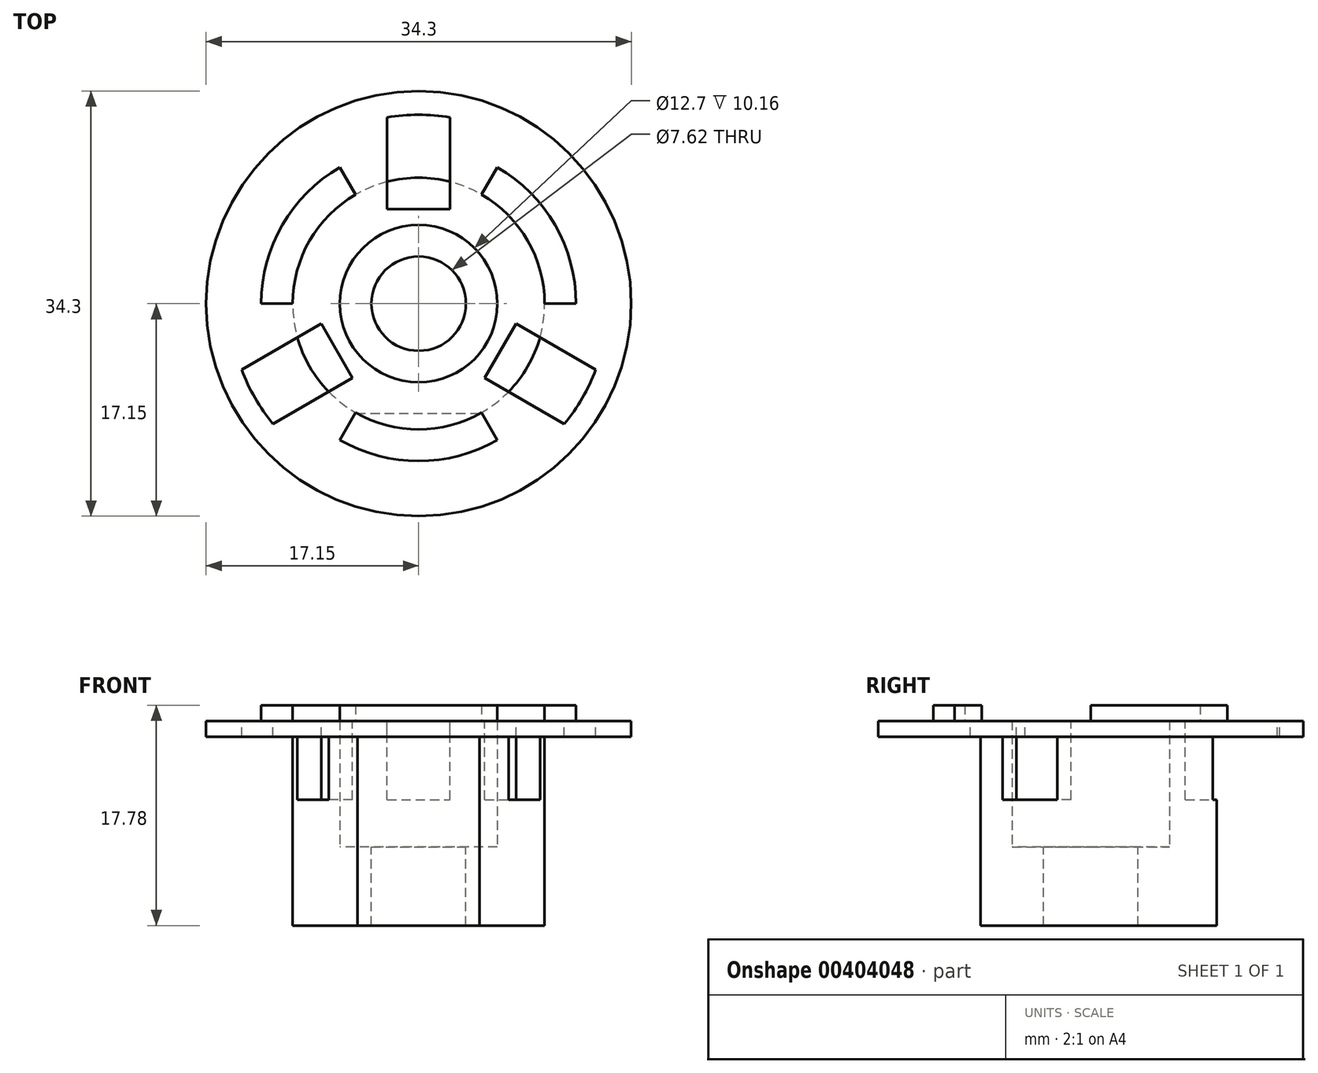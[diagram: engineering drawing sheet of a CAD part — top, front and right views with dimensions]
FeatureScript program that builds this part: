
annotation { "Feature Type Name" : "Feature", "Feature Type Description" : "" }
export const myFeature = defineFeature(function(context is Context, id is Id, definition is map)
    precondition{}
    {
        {
            var Q0;
            Q0=qCreatedBy(makeId("Top.planeOp"),FACE);
            var sketch = newSketch(context, id + "F0", { "sketchPlane" : qUnion([Q0])});
            skCircle(sketch, "E0", {"center": v(0, 0) * mm, "radius": 17.15 * mm});
            skCircle(sketch, "E1", {"center": v(0, 0) * mm, "radius": 6.35 * mm});
            skPoint(sketch, "E2", {"position": v(0, 8.9) * mm});
            skLineSegment(sketch, "E3.bottom", {"start": v(0, 8.9) * mm, "end": v(-2.54, 8.9) * mm});
            skLineSegment(sketch, "E3.top", {"start": v(0, 24.8) * mm, "end": v(-2.54, 24.8) * mm});
            skLineSegment(sketch, "E3.left", {"start": v(0, 8.9) * mm, "end": v(0, 24.8) * mm});
            skLineSegment(sketch, "E3.right", {"start": v(-2.54, 8.9) * mm, "end": v(-2.54, 24.8) * mm});
            skLineSegment(sketch, "E4.bottom", {"start": v(0, 8.9) * mm, "end": v(2.54, 8.9) * mm});
            skLineSegment(sketch, "E4.top", {"start": v(0, 24.8) * mm, "end": v(2.54, 24.8) * mm});
            skLineSegment(sketch, "E4.right", {"start": v(2.54, 8.9) * mm, "end": v(2.54, 24.8) * mm});
            skLineSegment(sketch, "E5.1.0", {"start": v(-6.43, -6.64) * mm, "end": v(-20.2, -14.6) * mm});
            skLineSegment(sketch, "E5.1.1", {"start": v(-21.47, -12.4) * mm, "end": v(-20.2, -14.6) * mm});
            skLineSegment(sketch, "E5.1.2", {"start": v(-21.47, -12.4) * mm, "end": v(-22.74, -10.2) * mm});
            skLineSegment(sketch, "E5.1.3", {"start": v(-8.97, -2.25) * mm, "end": v(-22.74, -10.2) * mm});
            skLineSegment(sketch, "E5.1.4", {"start": v(-7.7, -4.45) * mm, "end": v(-8.97, -2.25) * mm});
            skLineSegment(sketch, "E5.1.5", {"start": v(-7.7, -4.45) * mm, "end": v(-6.43, -6.64) * mm});
            skLineSegment(sketch, "E5.2.0", {"start": v(8.97, -2.25) * mm, "end": v(22.74, -10.2) * mm});
            skLineSegment(sketch, "E5.2.1", {"start": v(21.47, -12.4) * mm, "end": v(22.74, -10.2) * mm});
            skLineSegment(sketch, "E5.2.2", {"start": v(21.47, -12.4) * mm, "end": v(20.2, -14.6) * mm});
            skLineSegment(sketch, "E5.2.3", {"start": v(6.43, -6.64) * mm, "end": v(20.2, -14.6) * mm});
            skLineSegment(sketch, "E5.2.4", {"start": v(7.7, -4.44) * mm, "end": v(6.43, -6.64) * mm});
            skLineSegment(sketch, "E5.2.5", {"start": v(7.7, -4.44) * mm, "end": v(8.97, -2.25) * mm});
            skSolve(sketch);
        }
        {
            var Q0;
            Q0=makeQuery(id+"F0.imprint","IMPRINT",FACE,{"disambiguationData":[TD([[makeQuery(id+"F0.imprint","IMPRINT",EDGE,{"derivedFrom":sQuery(id+"F0.wireOp",EDGE,"E1")}),-1.0]])]});
            extrude(context, id + "F1", {"entities" : qUnion([Q0]), "depth" : 1.27 * mm});
        }
        {
            var Q0;
            Q0=makeQuery(id+"F1.opExtrude","CAP_FACE",FACE,{"disambiguationData":[OSD([sQuery(id+"F0.wireOp",EDGE,"E0"),sQuery(id+"F0.wireOp",EDGE,"E1"),sQuery(id+"F0.wireOp",EDGE,"E3.bottom"),sQuery(id+"F0.wireOp",EDGE,"E3.right"),sQuery(id+"F0.wireOp",EDGE,"E4.bottom"),sQuery(id+"F0.wireOp",EDGE,"E4.right"),sQuery(id+"F0.wireOp",EDGE,"E5.1.0"),sQuery(id+"F0.wireOp",EDGE,"E5.1.3"),sQuery(id+"F0.wireOp",EDGE,"E5.1.4"),sQuery(id+"F0.wireOp",EDGE,"E5.1.5"),sQuery(id+"F0.wireOp",EDGE,"E5.2.0"),sQuery(id+"F0.wireOp",EDGE,"E5.2.3"),sQuery(id+"F0.wireOp",EDGE,"E5.2.4"),sQuery(id+"F0.wireOp",EDGE,"E5.2.5")])],"isStart":true});
            var sketch = newSketch(context, id + "F2", { "sketchPlane" : qUnion([Q0])});
            skCircle(sketch, "E6", {"center": v(0, 0) * mm, "radius": 6.35 * mm});
            skCircle(sketch, "E7", {"center": v(0, 0) * mm, "radius": 10.16 * mm});
            skPoint(sketch, "E8", {"position": v(-2.54, -7.62) * mm});
            skLineSegment(sketch, "E9.bottom", {"start": v(-2.54, -7.62) * mm, "end": v(2.54, -7.62) * mm});
            skLineSegment(sketch, "E9.top", {"start": v(-2.54, -12.48) * mm, "end": v(2.54, -12.48) * mm});
            skLineSegment(sketch, "E9.left", {"start": v(-2.54, -7.62) * mm, "end": v(-2.54, -12.48) * mm});
            skLineSegment(sketch, "E9.right", {"start": v(2.54, -7.62) * mm, "end": v(2.54, -12.48) * mm});
            skLineSegment(sketch, "E10.1.0", {"start": v(7.87, 1.61) * mm, "end": v(5.33, 6) * mm});
            skLineSegment(sketch, "E10.1.1", {"start": v(7.87, 1.61) * mm, "end": v(12.07, 4.04) * mm});
            skLineSegment(sketch, "E10.1.2", {"start": v(12.07, 4.04) * mm, "end": v(9.53, 8.44) * mm});
            skLineSegment(sketch, "E10.1.3", {"start": v(5.33, 6) * mm, "end": v(9.53, 8.44) * mm});
            skLineSegment(sketch, "E10.2.0", {"start": v(-5.33, 6) * mm, "end": v(-7.87, 1.61) * mm});
            skLineSegment(sketch, "E10.2.1", {"start": v(-5.33, 6) * mm, "end": v(-9.53, 8.44) * mm});
            skLineSegment(sketch, "E10.2.2", {"start": v(-9.53, 8.44) * mm, "end": v(-12.07, 4.04) * mm});
            skLineSegment(sketch, "E10.2.3", {"start": v(-7.87, 1.61) * mm, "end": v(-12.07, 4.04) * mm});
            skSolve(sketch);
        }
        {
            var Q0;
            Q0=makeQuery(id+"F2.imprint","IMPRINT",FACE,{"disambiguationData":[TD([[makeQuery(id+"F2.imprint","IMPRINT",EDGE,{"derivedFrom":sQuery(id+"F2.wireOp",EDGE,"E6")}),1.0]])]});
            extrude(context, id + "F3", {"entities" : qUnion([Q0]), "operationType" : NewBodyOperationType.ADD, "depth" : 5.08 * mm});
        }
        {
            var Q0;
            Q0=makeQuery(id+"F3.opExtrude","CAP_FACE",FACE,{"disambiguationData":[OSD([sQuery(id+"F2.wireOp",EDGE,"E6"),sQuery(id+"F2.wireOp",EDGE,"E7"),sQuery(id+"F2.wireOp",EDGE,"E9.bottom"),sQuery(id+"F2.wireOp",EDGE,"E9.left"),sQuery(id+"F2.wireOp",EDGE,"E9.right"),sQuery(id+"F2.wireOp",EDGE,"E10.1.0"),sQuery(id+"F2.wireOp",EDGE,"E10.1.1"),sQuery(id+"F2.wireOp",EDGE,"E10.1.3"),sQuery(id+"F2.wireOp",EDGE,"E10.2.0"),sQuery(id+"F2.wireOp",EDGE,"E10.2.1"),sQuery(id+"F2.wireOp",EDGE,"E10.2.3")])],"isStart":false});
            var sketch = newSketch(context, id + "F4", { "sketchPlane" : qUnion([Q0])});
            skSolve(sketch);
        }
        {
            var Q0;
            Q0=makeQuery(id+"F4.imprint","IMPRINT",FACE,{"disambiguationData":[TD([[makeQuery(id+"F4.imprint","IMPRINT",EDGE,{"derivedFrom":makeQuery(id+"F3.opExtrude","CAP_EDGE",EDGE,{"disambiguationData":[OSD([sQuery(id+"F2.wireOp",EDGE,"E6")])],"isStart":false})}),1.0]])]});
            var sketch = newSketch(context, id + "F5", { "sketchPlane" : qUnion([Q0])});
            skCircle(sketch, "E11", {"center": v(0, 0) * mm, "radius": 6.35 * mm});
            skCircle(sketch, "E12", {"center": v(0, 0) * mm, "radius": 10.16 * mm});
            skSolve(sketch);
        }
        {
            var Q0;
            Q0=makeQuery(id+"F4.imprint","IMPRINT",FACE,{"disambiguationData":[TD([[makeQuery(id+"F4.imprint","IMPRINT",EDGE,{"derivedFrom":makeQuery(id+"F3.opExtrude","CAP_EDGE",EDGE,{"disambiguationData":[OSD([sQuery(id+"F2.wireOp",EDGE,"E6")])],"isStart":false})}),1.0]])]});
            var Q1;
            Q1=makeQuery(id+"F5.imprint","IMPRINT",FACE,{"disambiguationData":[TD([[makeQuery(id+"F5.imprint","IMPRINT",EDGE,{"derivedFrom":makeQuery(id+"F4.imprint","IMPRINT",EDGE,{"derivedFrom":makeQuery(id+"F3.opExtrude","CAP_EDGE",EDGE,{"disambiguationData":[OSD([sQuery(id+"F2.wireOp",EDGE,"E10.2.0")])],"isStart":false})})}),-1.0]])]});
            var Q2;
            Q2=makeQuery(id+"F5.imprint","IMPRINT",FACE,{"disambiguationData":[TD([[makeQuery(id+"F5.imprint","IMPRINT",EDGE,{"derivedFrom":makeQuery(id+"F4.imprint","IMPRINT",EDGE,{"derivedFrom":makeQuery(id+"F3.opExtrude","CAP_EDGE",EDGE,{"disambiguationData":[OSD([sQuery(id+"F2.wireOp",EDGE,"E10.1.0")])],"isStart":false})})}),-1.0]])]});
            var Q3;
            Q3=makeQuery(id+"F5.imprint","IMPRINT",FACE,{"disambiguationData":[TD([[makeQuery(id+"F5.imprint","IMPRINT",EDGE,{"derivedFrom":makeQuery(id+"F4.imprint","IMPRINT",EDGE,{"derivedFrom":makeQuery(id+"F3.opExtrude","CAP_EDGE",EDGE,{"disambiguationData":[OSD([sQuery(id+"F2.wireOp",EDGE,"E9.bottom")])],"isStart":false})})}),-1.0]])]});
            extrude(context, id + "F6", {"entities" : qUnion([Q0, Q1, Q2, Q3]), "operationType" : NewBodyOperationType.ADD, "depth" : 3.8 * mm});
        }
        {
            var Q0;
            {var subQ0=sQuery(id+"F5.wireOp",EDGE,"E12");var subQ1=sQuery(id+"F2.wireOp",EDGE,"E9.right");var subQ2=sQuery(id+"F2.wireOp",EDGE,"E9.left");var subQ3=sQuery(id+"F2.wireOp",EDGE,"E9.bottom");var subQ4=sQuery(id+"F2.wireOp",EDGE,"E10.2.3");var subQ5=sQuery(id+"F2.wireOp",EDGE,"E10.2.1");var subQ6=sQuery(id+"F2.wireOp",EDGE,"E10.2.0");var subQ7=sQuery(id+"F2.wireOp",EDGE,"E10.1.3");var subQ8=sQuery(id+"F2.wireOp",EDGE,"E10.1.1");var subQ9=sQuery(id+"F2.wireOp",EDGE,"E10.1.0");Q0=makeQuery(id+"F6.boolean.opBoolean","MERGE",FACE,{"derivedFrom":[makeQuery(id+"F6.opExtrude","CAP_FACE",FACE,{"disambiguationData":[OSD([sQuery(id+"F2.wireOp",EDGE,"E6"),sQuery(id+"F2.wireOp",EDGE,"E7"),subQ3,subQ2,subQ1,subQ9,subQ8,subQ7,subQ6,subQ5,subQ4])],"isStart":false}),makeQuery(id+"F6.opExtrude","CAP_FACE",FACE,{"disambiguationData":[OSD([subQ9,subQ8,subQ7,subQ0])],"isStart":false}),makeQuery(id+"F6.opExtrude","CAP_FACE",FACE,{"disambiguationData":[OSD([subQ6,subQ5,subQ4,subQ0])],"isStart":false}),makeQuery(id+"F6.opExtrude","CAP_FACE",FACE,{"disambiguationData":[OSD([subQ3,subQ2,subQ1,subQ0])],"isStart":false})]});}
            var sketch = newSketch(context, id + "F7", { "sketchPlane" : qUnion([Q0])});
            skCircle(sketch, "E13", {"center": v(0, 0) * mm, "radius": 3.81 * mm});
            skCircle(sketch, "E14", {"center": v(0, 0) * mm, "radius": 10.16 * mm});
            skSolve(sketch);
        }
        {
            var Q0;
            Q0=makeQuery(id+"F7.imprint","IMPRINT",FACE,{"disambiguationData":[TD([[makeQuery(id+"F7.imprint","IMPRINT",EDGE,{"derivedFrom":sQuery(id+"F7.wireOp",EDGE,"E13")}),-1.0]])]});
            var Q1;
            Q1=makeQuery(id+"F7.imprint","IMPRINT",FACE,{"disambiguationData":[TD([[makeQuery(id+"F7.imprint","IMPRINT",EDGE,{"derivedFrom":sQuery(id+"F7.wireOp",EDGE,"E14")}),1.0]])]});
            extrude(context, id + "F8", {"entities" : qUnion([Q0, Q1]), "operationType" : NewBodyOperationType.ADD, "depth" : 6.35 * mm});
        }
        {
            var Q0;
            Q0=makeQuery(id+"F8.opExtrude","CAP_FACE",FACE,{"disambiguationData":[OSD([sQuery(id+"F7.wireOp",EDGE,"E13"),sQuery(id+"F7.wireOp",EDGE,"E14")])],"isStart":false});
            var sketch = newSketch(context, id + "F9", { "sketchPlane" : qUnion([Q0])});
            skLineSegment(sketch, "E15.bottom", {"start": v(12.8, 8.9) * mm, "end": v(-12.8, 8.9) * mm});
            skLineSegment(sketch, "E15.top", {"start": v(12.8, 11.43) * mm, "end": v(-12.8, 11.43) * mm});
            skLineSegment(sketch, "E15.left", {"start": v(12.8, 8.9) * mm, "end": v(12.8, 11.43) * mm});
            skLineSegment(sketch, "E15.right", {"start": v(-12.8, 8.9) * mm, "end": v(-12.8, 11.43) * mm});
            skPoint(sketch, "E15.middle", {"position": v(0, 10.16) * mm});
            skSolve(sketch);
        }
        {
            var Q0;
            Q0=makeQuery(id+"F9.imprint","IMPRINT",FACE,{"disambiguationData":[TD([[makeQuery(id+"F9.imprint","IMPRINT",EDGE,{"derivedFrom":sQuery(id+"F9.wireOp",EDGE,"E15.top")}),1.0]])]});
            var Q1;
            {var subQ0=sQuery(id+"F9.wireOp",EDGE,"E15.bottom");var subQ1=makeQuery(id+"F8.opExtrude","CAP_EDGE",EDGE,{"disambiguationData":[OSD([sQuery(id+"F7.wireOp",EDGE,"E14")])],"isStart":false});var subQ2=makeQuery(id+"F9.imprint","INTERSECT",VERTEX,{"disambiguationData":[OD(0.0)],"derivedFrom":[subQ1,subQ0]});Q1=makeQuery(id+"F9.imprint","IMPRINT",FACE,{"disambiguationData":[TD([[makeQuery(id+"F9.imprint","IMPRINT",EDGE,{"disambiguationData":[TD([[subQ2,-1.0]])],"derivedFrom":subQ0}),-1.0]])]});}
            var Q2;
            {var subQ3=sQuery(id+"F0.wireOp",EDGE,"E5.1.0");var subQ4=sQuery(id+"F0.wireOp",EDGE,"E5.2.3");var subQ5=sQuery(id+"F0.wireOp",EDGE,"E0");Q2=makeQuery(id+"F3.boolean.opBoolean","SPLIT",FACE,{"disambiguationData":[TD([makeQuery(id+"F1.opExtrude","SWEPT_FACE",FACE,{"disambiguationData":[OSD([subQ5]),TDD([makeQuery(id+"F0.imprint","IMPRINT",EDGE,{"disambiguationData":[TD([[makeQuery(id+"F0.imprint","INTERSECT",VERTEX,{"derivedFrom":[subQ5,subQ3]}),-1.0]])],"derivedFrom":subQ5})])]})])],"derivedFrom":makeQuery(id+"F1.opExtrude","CAP_FACE",FACE,{"disambiguationData":[OSD([subQ5,sQuery(id+"F0.wireOp",EDGE,"E1"),sQuery(id+"F0.wireOp",EDGE,"E3.bottom"),sQuery(id+"F0.wireOp",EDGE,"E3.right"),sQuery(id+"F0.wireOp",EDGE,"E4.bottom"),sQuery(id+"F0.wireOp",EDGE,"E4.right"),subQ3,sQuery(id+"F0.wireOp",EDGE,"E5.1.3"),sQuery(id+"F0.wireOp",EDGE,"E5.1.4"),sQuery(id+"F0.wireOp",EDGE,"E5.1.5"),sQuery(id+"F0.wireOp",EDGE,"E5.2.0"),subQ4,sQuery(id+"F0.wireOp",EDGE,"E5.2.4"),sQuery(id+"F0.wireOp",EDGE,"E5.2.5")])],"isStart":true})});}
            extrude(context, id + "F10", {"entities" : qUnion([Q0, Q1]), "operationType" : NewBodyOperationType.REMOVE, "endBound" : BoundingType.UP_TO_SURFACE, "oppositeDirection" : true, "endBoundEntityFace" : qUnion([Q2]), "depth" : 25.4 * mm});
        }
        {
            var Q0;
            {var subQ0=sQuery(id+"F0.wireOp",EDGE,"E3.right");var subQ1=sQuery(id+"F0.wireOp",EDGE,"E4.right");var subQ2=sQuery(id+"F0.wireOp",EDGE,"E4.bottom");var subQ3=sQuery(id+"F0.wireOp",EDGE,"E3.bottom");Q0=makeQuery(id+"F3.boolean.opBoolean","SPLIT",FACE,{"disambiguationData":[TD([makeQuery(id+"F3.opExtrude","SWEPT_FACE",FACE,{"disambiguationData":[OSD([sQuery(id+"F2.wireOp",EDGE,"E9.bottom")])]})])],"derivedFrom":makeQuery(id+"F1.opExtrude","CAP_FACE",FACE,{"disambiguationData":[OSD([sQuery(id+"F0.wireOp",EDGE,"E0"),sQuery(id+"F0.wireOp",EDGE,"E1"),subQ3,subQ0,subQ2,subQ1,sQuery(id+"F0.wireOp",EDGE,"E5.1.0"),sQuery(id+"F0.wireOp",EDGE,"E5.1.3"),sQuery(id+"F0.wireOp",EDGE,"E5.1.4"),sQuery(id+"F0.wireOp",EDGE,"E5.1.5"),sQuery(id+"F0.wireOp",EDGE,"E5.2.0"),sQuery(id+"F0.wireOp",EDGE,"E5.2.3"),sQuery(id+"F0.wireOp",EDGE,"E5.2.4"),sQuery(id+"F0.wireOp",EDGE,"E5.2.5")])],"isStart":true})});}
            var sketch = newSketch(context, id + "F11", { "sketchPlane" : qUnion([Q0])});
            skLineSegment(sketch, "E16.bottom", {"start": v(-2.54, -7.62) * mm, "end": v(2.54, -7.62) * mm});
            skLineSegment(sketch, "E16.top", {"start": v(-2.54, -8.9) * mm, "end": v(2.54, -8.9) * mm});
            skLineSegment(sketch, "E16.left", {"start": v(-2.54, -7.62) * mm, "end": v(-2.54, -8.9) * mm});
            skLineSegment(sketch, "E16.right", {"start": v(2.54, -7.62) * mm, "end": v(2.54, -8.9) * mm});
            skLineSegment(sketch, "E17.1.0", {"start": v(8.97, 2.25) * mm, "end": v(6.43, 6.64) * mm});
            skLineSegment(sketch, "E17.1.1", {"start": v(7.87, 1.61) * mm, "end": v(5.33, 6) * mm});
            skLineSegment(sketch, "E17.1.2", {"start": v(7.87, 1.61) * mm, "end": v(8.97, 2.25) * mm});
            skLineSegment(sketch, "E17.1.3", {"start": v(5.33, 6) * mm, "end": v(6.43, 6.64) * mm});
            skLineSegment(sketch, "E17.2.0", {"start": v(-6.43, 6.64) * mm, "end": v(-8.97, 2.25) * mm});
            skLineSegment(sketch, "E17.2.1", {"start": v(-5.33, 6) * mm, "end": v(-7.87, 1.61) * mm});
            skLineSegment(sketch, "E17.2.2", {"start": v(-5.33, 6) * mm, "end": v(-6.43, 6.64) * mm});
            skLineSegment(sketch, "E17.2.3", {"start": v(-7.87, 1.61) * mm, "end": v(-8.97, 2.25) * mm});
            skPoint(sketch, "E17.center", {"position": v(0, 0) * mm});
            skSolve(sketch);
        }
        {
            var Q0;
            Q0=makeQuery(id+"F11.imprint","IMPRINT",FACE,{"disambiguationData":[TD([[makeQuery(id+"F11.imprint","IMPRINT",EDGE,{"derivedFrom":sQuery(id+"F11.wireOp",EDGE,"E16.bottom")}),-1.0]])]});
            var Q1;
            Q1=makeQuery(id+"F11.imprint","IMPRINT",FACE,{"disambiguationData":[TD([[makeQuery(id+"F11.imprint","IMPRINT",EDGE,{"derivedFrom":sQuery(id+"F11.wireOp",EDGE,"E17.1.0")}),1.0]])]});
            var Q2;
            Q2=makeQuery(id+"F11.imprint","IMPRINT",FACE,{"disambiguationData":[TD([[makeQuery(id+"F11.imprint","IMPRINT",EDGE,{"derivedFrom":sQuery(id+"F11.wireOp",EDGE,"E17.2.0")}),1.0]])]});
            extrude(context, id + "F12", {"entities" : qUnion([Q0, Q1, Q2]), "operationType" : NewBodyOperationType.REMOVE, "oppositeDirection" : true, "depth" : 25.4 * mm});
        }
        {
            var Q0;
            Q0=makeQuery(id+"F1.opExtrude","CAP_FACE",FACE,{"disambiguationData":[OSD([sQuery(id+"F0.wireOp",EDGE,"E0"),sQuery(id+"F0.wireOp",EDGE,"E1"),sQuery(id+"F0.wireOp",EDGE,"E3.bottom"),sQuery(id+"F0.wireOp",EDGE,"E3.right"),sQuery(id+"F0.wireOp",EDGE,"E4.bottom"),sQuery(id+"F0.wireOp",EDGE,"E4.right"),sQuery(id+"F0.wireOp",EDGE,"E5.1.0"),sQuery(id+"F0.wireOp",EDGE,"E5.1.3"),sQuery(id+"F0.wireOp",EDGE,"E5.1.4"),sQuery(id+"F0.wireOp",EDGE,"E5.1.5"),sQuery(id+"F0.wireOp",EDGE,"E5.2.0"),sQuery(id+"F0.wireOp",EDGE,"E5.2.3"),sQuery(id+"F0.wireOp",EDGE,"E5.2.4"),sQuery(id+"F0.wireOp",EDGE,"E5.2.5")])],"isStart":false});
            var sketch = newSketch(context, id + "F13", { "sketchPlane" : qUnion([Q0])});
            skCircle(sketch, "E18", {"center": v(0, 0) * mm, "radius": 17.15 * mm});
            skCircle(sketch, "E19", {"center": v(0, 0) * mm, "radius": 15.24 * mm});
            skSolve(sketch);
        }
        {
            var Q0;
            {var subQ0=sQuery(id+"F13.wireOp",EDGE,"E18");var subQ1=makeQuery(id+"F1.opExtrude","CAP_FACE",FACE,{"disambiguationData":[OSD([sQuery(id+"F0.wireOp",EDGE,"E0"),sQuery(id+"F0.wireOp",EDGE,"E1"),sQuery(id+"F0.wireOp",EDGE,"E3.bottom"),sQuery(id+"F0.wireOp",EDGE,"E3.right"),sQuery(id+"F0.wireOp",EDGE,"E4.bottom"),sQuery(id+"F0.wireOp",EDGE,"E4.right"),sQuery(id+"F0.wireOp",EDGE,"E5.1.0"),sQuery(id+"F0.wireOp",EDGE,"E5.1.3"),sQuery(id+"F0.wireOp",EDGE,"E5.1.4"),sQuery(id+"F0.wireOp",EDGE,"E5.1.5"),sQuery(id+"F0.wireOp",EDGE,"E5.2.0"),sQuery(id+"F0.wireOp",EDGE,"E5.2.3"),sQuery(id+"F0.wireOp",EDGE,"E5.2.4"),sQuery(id+"F0.wireOp",EDGE,"E5.2.5")])],"isStart":false});var subQ2=makeQuery(id+"F12.boolean.opBoolean","INTERSECT",EDGE,{"derivedFrom":[subQ1,makeQuery(id+"F12.opExtrude","SWEPT_FACE",FACE,{"disambiguationData":[OSD([sQuery(id+"F11.wireOp",EDGE,"E16.right")])]})]});var subQ3=makeQuery(id+"F13.imprint","INTERSECT",VERTEX,{"derivedFrom":[subQ2,subQ0]});Q0=makeQuery(id+"F13.imprint","IMPRINT",FACE,{"disambiguationData":[TD([[makeQuery(id+"F13.imprint","IMPRINT",EDGE,{"disambiguationData":[TD([[subQ3,-1.0]])],"derivedFrom":subQ0}),1.0]])]});}
            var Q1;
            {var subQ0=sQuery(id+"F13.wireOp",EDGE,"E18");var subQ1=makeQuery(id+"F1.opExtrude","CAP_FACE",FACE,{"disambiguationData":[OSD([sQuery(id+"F0.wireOp",EDGE,"E0"),sQuery(id+"F0.wireOp",EDGE,"E1"),sQuery(id+"F0.wireOp",EDGE,"E3.bottom"),sQuery(id+"F0.wireOp",EDGE,"E3.right"),sQuery(id+"F0.wireOp",EDGE,"E4.bottom"),sQuery(id+"F0.wireOp",EDGE,"E4.right"),sQuery(id+"F0.wireOp",EDGE,"E5.1.0"),sQuery(id+"F0.wireOp",EDGE,"E5.1.3"),sQuery(id+"F0.wireOp",EDGE,"E5.1.4"),sQuery(id+"F0.wireOp",EDGE,"E5.1.5"),sQuery(id+"F0.wireOp",EDGE,"E5.2.0"),sQuery(id+"F0.wireOp",EDGE,"E5.2.3"),sQuery(id+"F0.wireOp",EDGE,"E5.2.4"),sQuery(id+"F0.wireOp",EDGE,"E5.2.5")])],"isStart":false});var subQ2=makeQuery(id+"F12.boolean.opBoolean","INTERSECT",EDGE,{"derivedFrom":[subQ1,makeQuery(id+"F12.opExtrude","SWEPT_FACE",FACE,{"disambiguationData":[OSD([sQuery(id+"F11.wireOp",EDGE,"E17.2.3")])]})]});var subQ3=makeQuery(id+"F13.imprint","INTERSECT",VERTEX,{"derivedFrom":[subQ2,subQ0]});Q1=makeQuery(id+"F13.imprint","IMPRINT",FACE,{"disambiguationData":[TD([[makeQuery(id+"F13.imprint","IMPRINT",EDGE,{"disambiguationData":[TD([[subQ3,-1.0]])],"derivedFrom":subQ0}),1.0]])]});}
            var Q2;
            {var subQ0=sQuery(id+"F13.wireOp",EDGE,"E18");var subQ1=makeQuery(id+"F1.opExtrude","CAP_FACE",FACE,{"disambiguationData":[OSD([sQuery(id+"F0.wireOp",EDGE,"E0"),sQuery(id+"F0.wireOp",EDGE,"E1"),sQuery(id+"F0.wireOp",EDGE,"E3.bottom"),sQuery(id+"F0.wireOp",EDGE,"E3.right"),sQuery(id+"F0.wireOp",EDGE,"E4.bottom"),sQuery(id+"F0.wireOp",EDGE,"E4.right"),sQuery(id+"F0.wireOp",EDGE,"E5.1.0"),sQuery(id+"F0.wireOp",EDGE,"E5.1.3"),sQuery(id+"F0.wireOp",EDGE,"E5.1.4"),sQuery(id+"F0.wireOp",EDGE,"E5.1.5"),sQuery(id+"F0.wireOp",EDGE,"E5.2.0"),sQuery(id+"F0.wireOp",EDGE,"E5.2.3"),sQuery(id+"F0.wireOp",EDGE,"E5.2.4"),sQuery(id+"F0.wireOp",EDGE,"E5.2.5")])],"isStart":false});var subQ2=makeQuery(id+"F12.boolean.opBoolean","INTERSECT",EDGE,{"derivedFrom":[subQ1,makeQuery(id+"F12.opExtrude","SWEPT_FACE",FACE,{"disambiguationData":[OSD([sQuery(id+"F11.wireOp",EDGE,"E17.1.3")])]})]});var subQ3=makeQuery(id+"F13.imprint","INTERSECT",VERTEX,{"derivedFrom":[subQ2,subQ0]});Q2=makeQuery(id+"F13.imprint","IMPRINT",FACE,{"disambiguationData":[TD([[makeQuery(id+"F13.imprint","IMPRINT",EDGE,{"disambiguationData":[TD([[subQ3,-1.0]])],"derivedFrom":subQ0}),1.0]])]});}
            extrude(context, id + "F14", {"entities" : qUnion([Q0, Q1, Q2]), "operationType" : NewBodyOperationType.ADD, "oppositeDirection" : true, "depth" : 1.27 * mm});
        }
        {
            var Q0;
            {var subQ0=sQuery(id+"F13.wireOp",EDGE,"E19");var subQ1=sQuery(id+"F13.wireOp",EDGE,"E18");var subQ2=sQuery(id+"F0.wireOp",EDGE,"E5.2.5");var subQ3=sQuery(id+"F0.wireOp",EDGE,"E5.2.4");var subQ4=sQuery(id+"F0.wireOp",EDGE,"E5.2.3");var subQ5=sQuery(id+"F0.wireOp",EDGE,"E5.2.0");var subQ6=sQuery(id+"F0.wireOp",EDGE,"E5.1.5");var subQ7=sQuery(id+"F0.wireOp",EDGE,"E5.1.4");var subQ8=sQuery(id+"F0.wireOp",EDGE,"E5.1.3");var subQ9=sQuery(id+"F0.wireOp",EDGE,"E5.1.0");var subQ10=sQuery(id+"F0.wireOp",EDGE,"E4.right");var subQ11=sQuery(id+"F0.wireOp",EDGE,"E4.bottom");var subQ12=sQuery(id+"F0.wireOp",EDGE,"E3.right");var subQ13=sQuery(id+"F0.wireOp",EDGE,"E3.bottom");var subQ14=sQuery(id+"F0.wireOp",EDGE,"E1");var subQ15=sQuery(id+"F0.wireOp",EDGE,"E0");Q0=makeQuery(id+"F14.boolean.opBoolean","MERGE",FACE,{"derivedFrom":[makeQuery(id+"F1.opExtrude","CAP_FACE",FACE,{"disambiguationData":[OSD([subQ15,subQ14,subQ13,subQ12,subQ11,subQ10,subQ9,subQ8,subQ7,subQ6,subQ5,subQ4,subQ3,subQ2])],"isStart":false}),makeQuery(id+"F14.opExtrude","CAP_FACE",FACE,{"disambiguationData":[OSD([subQ15,subQ14,subQ13,subQ12,subQ11,subQ10,subQ9,subQ8,subQ7,subQ6,subQ5,subQ4,subQ3,subQ2,sQuery(id+"F11.wireOp",EDGE,"E16.left"),sQuery(id+"F11.wireOp",EDGE,"E16.right"),subQ1,subQ0])],"isStart":true}),makeQuery(id+"F14.opExtrude","CAP_FACE",FACE,{"disambiguationData":[OSD([subQ15,subQ14,subQ13,subQ12,subQ11,subQ10,subQ9,subQ8,subQ7,subQ6,subQ5,subQ4,subQ3,subQ2,sQuery(id+"F11.wireOp",EDGE,"E17.2.2"),sQuery(id+"F11.wireOp",EDGE,"E17.2.3"),subQ1,subQ0])],"isStart":true}),makeQuery(id+"F14.opExtrude","CAP_FACE",FACE,{"disambiguationData":[OSD([subQ15,subQ14,subQ13,subQ12,subQ11,subQ10,subQ9,subQ8,subQ7,subQ6,subQ5,subQ4,subQ3,subQ2,sQuery(id+"F11.wireOp",EDGE,"E17.1.2"),sQuery(id+"F11.wireOp",EDGE,"E17.1.3"),subQ1,subQ0])],"isStart":true})]});}
            var sketch = newSketch(context, id + "F15", { "sketchPlane" : qUnion([Q0])});
            skCircle(sketch, "E20", {"center": v(0, 0) * mm, "radius": 12.7 * mm});
            skCircle(sketch, "E21", {"center": v(0, 0) * mm, "radius": 10.16 * mm});
            skLineSegment(sketch, "E22", {"start": v(0, 0) * mm, "end": v(-6.35, -11) * mm});
            skLineSegment(sketch, "E23", {"start": v(0, 0) * mm, "end": v(6.35, -11) * mm});
            skLineSegment(sketch, "E24.1.0", {"start": v(0, 0) * mm, "end": v(12.7, 0) * mm});
            skLineSegment(sketch, "E24.1.1", {"start": v(0, 0) * mm, "end": v(6.35, 11) * mm});
            skLineSegment(sketch, "E24.2.0", {"start": v(0, 0) * mm, "end": v(-6.35, 11) * mm});
            skLineSegment(sketch, "E24.2.1", {"start": v(0, 0) * mm, "end": v(-12.7, 0) * mm});
            skSolve(sketch);
        }
        {
            var Q0;
            {var subQ0=sQuery(id+"F15.wireOp",EDGE,"E24.2.0");var subQ1=sQuery(id+"F15.wireOp",EDGE,"E20");var subQ2=makeQuery(id+"F15.imprint","INTERSECT",VERTEX,{"derivedFrom":[subQ1,subQ0]});Q0=makeQuery(id+"F15.imprint","IMPRINT",FACE,{"disambiguationData":[TD([[makeQuery(id+"F15.imprint","IMPRINT",EDGE,{"disambiguationData":[TD([[subQ2,-1.0]])],"derivedFrom":subQ1}),1.0]])]});}
            var Q1;
            {var subQ0=sQuery(id+"F15.wireOp",EDGE,"E24.1.0");var subQ1=sQuery(id+"F15.wireOp",EDGE,"E20");var subQ2=makeQuery(id+"F15.imprint","INTERSECT",VERTEX,{"derivedFrom":[subQ1,subQ0]});Q1=makeQuery(id+"F15.imprint","IMPRINT",FACE,{"disambiguationData":[TD([[makeQuery(id+"F15.imprint","IMPRINT",EDGE,{"disambiguationData":[TD([[subQ2,-1.0]])],"derivedFrom":subQ1}),1.0]])]});}
            var Q2;
            {var subQ0=sQuery(id+"F15.wireOp",EDGE,"E22");var subQ1=sQuery(id+"F15.wireOp",EDGE,"E20");var subQ2=makeQuery(id+"F15.imprint","INTERSECT",VERTEX,{"derivedFrom":[subQ1,subQ0]});Q2=makeQuery(id+"F15.imprint","IMPRINT",FACE,{"disambiguationData":[TD([[makeQuery(id+"F15.imprint","IMPRINT",EDGE,{"disambiguationData":[TD([[subQ2,-1.0]])],"derivedFrom":subQ1}),1.0]])]});}
            extrude(context, id + "F16", {"entities" : qUnion([Q0, Q1, Q2]), "operationType" : NewBodyOperationType.ADD, "depth" : 1.27 * mm});
        }
    });
